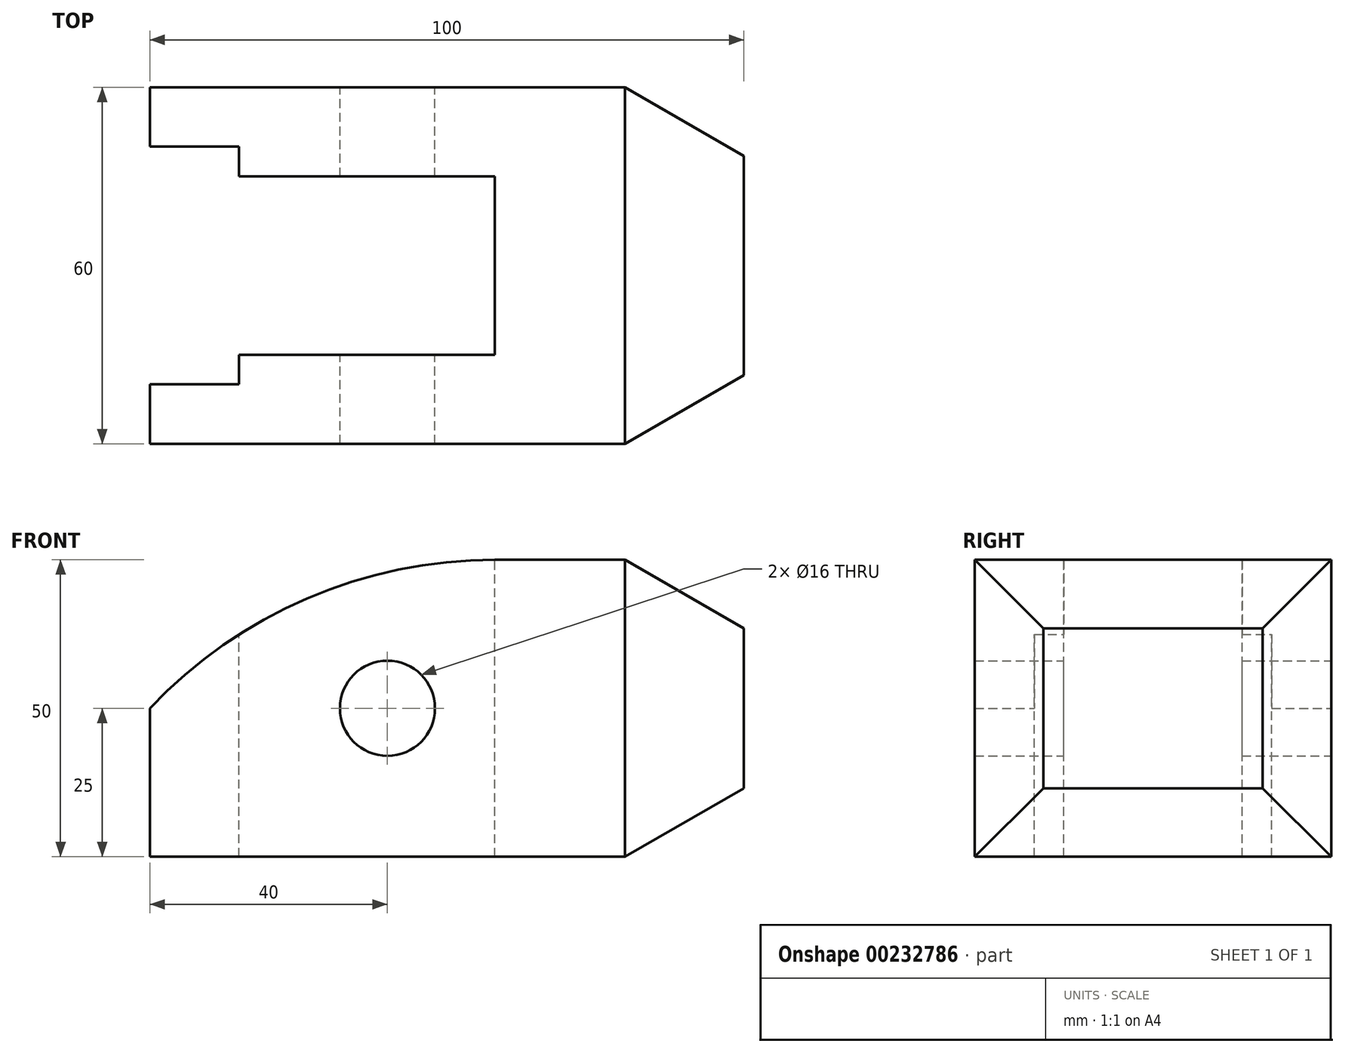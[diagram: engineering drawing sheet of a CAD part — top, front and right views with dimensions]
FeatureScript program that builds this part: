
annotation { "Feature Type Name" : "Feature", "Feature Type Description" : "" }
export const myFeature = defineFeature(function(context is Context, id is Id, definition is map)
    precondition{}
    {
        {
            var Q0;
            Q0=qCreatedBy(makeId("Front.planeOp"),FACE);
            var sketch = newSketch(context, id + "F0", { "sketchPlane" : qUnion([Q0])});
            skLineSegment(sketch, "E0.bottom", {"start": v(0, 0) * mm, "end": v(-80, 0) * mm});
            skLineSegment(sketch, "E0.top", {"start": v(0, 50) * mm, "end": v(-21.9, 50) * mm});
            skLineSegment(sketch, "E0.left", {"start": v(0, 0) * mm, "end": v(0, 50) * mm});
            skLineSegment(sketch, "E0.right", {"start": v(-80, 0) * mm, "end": v(-80, 25) * mm});
            skCircle(sketch, "E1", {"center": v(-40, 25) * mm, "radius": 8 * mm});
            skArc(sketch, "E2", {"start": v(-21.9, 50) * mm, "mid": v(-53.53, 43.48) * mm, "end": v(-80, 25) * mm});
            skLineSegment(sketch, "E3", {"start": v(-80, 25) * mm, "end": v(0, 25) * mm, "construction": true});
            skSolve(sketch);
        }
        {
            var Q0;
            Q0 = qSketchRegion(id + "F0", true);
            extrude(context, id + "F1", {"entities" : qUnion([Q0]), "depth" : 60 * mm});
        }
        {
            var Q0;
            Q0=makeQuery(id+"F1.opExtrude","SWEPT_FACE",FACE,{"disambiguationData":[OSD([sQuery(id+"F0.wireOp",EDGE,"E0.top")])]});
            var sketch = newSketch(context, id + "F2", { "sketchPlane" : qUnion([Q0])});
            skLineSegment(sketch, "E4.0", {"start": v(0, 0) * mm, "end": v(-21.9, 0) * mm, "construction": true});
            skLineSegment(sketch, "E5.0.0", {"start": v(-21.9, 0) * mm, "end": v(-80, 0) * mm, "construction": true});
            skLineSegment(sketch, "E5.0.1", {"start": v(-80, 0) * mm, "end": v(-80, -60) * mm, "construction": true});
            skLineSegment(sketch, "E5.0.2", {"start": v(-80, -60) * mm, "end": v(-21.9, -60) * mm, "construction": true});
            skLineSegment(sketch, "E5.0.3", {"start": v(-21.9, -60) * mm, "end": v(-21.9, 0) * mm, "construction": true});
            skLineSegment(sketch, "E6.0.1", {"start": v(-21.9, 0) * mm, "end": v(-21.9, -60) * mm, "construction": true});
            skLineSegment(sketch, "E6.0.2", {"start": v(-21.9, -60) * mm, "end": v(0, -60) * mm, "construction": true});
            skLineSegment(sketch, "E6.0.3", {"start": v(0, -60) * mm, "end": v(0, 0) * mm, "construction": true});
            skLineSegment(sketch, "E7", {"start": v(0, -30) * mm, "end": v(-80, -30) * mm, "construction": true});
            skLineSegment(sketch, "E8.bottom", {"start": v(-80, -15) * mm, "end": v(-15, -15) * mm});
            skLineSegment(sketch, "E8.top", {"start": v(-80, -45) * mm, "end": v(-15, -45) * mm});
            skLineSegment(sketch, "E8.left", {"start": v(-80, -15) * mm, "end": v(-80, -45) * mm});
            skLineSegment(sketch, "E8.right", {"start": v(-15, -15) * mm, "end": v(-15, -45) * mm});
            skLineSegment(sketch, "E9.top", {"start": v(-80, -10) * mm, "end": v(-65, -10) * mm});
            skLineSegment(sketch, "E9.left", {"start": v(-80, -15) * mm, "end": v(-80, -10) * mm});
            skLineSegment(sketch, "E9.right", {"start": v(-65, -15) * mm, "end": v(-65, -10) * mm});
            skLineSegment(sketch, "E10.top", {"start": v(-80, -50) * mm, "end": v(-65, -50) * mm});
            skLineSegment(sketch, "E10.left", {"start": v(-80, -45) * mm, "end": v(-80, -50) * mm});
            skLineSegment(sketch, "E10.right", {"start": v(-65, -45) * mm, "end": v(-65, -50) * mm});
            skSolve(sketch);
        }
        {
            var Q0;
            Q0=makeQuery(id+"F2.imprint","IMPRINT",FACE,{"disambiguationData":[TD([[makeQuery(id+"F2.imprint","IMPRINT",EDGE,{"derivedFrom":sQuery(id+"F2.wireOp",EDGE,"E9.top")}),-1.0]])]});
            var Q1;
            {var subQ4=sQuery(id+"F2.wireOp",EDGE,"E8.left");Q1=makeQuery(id+"F2.imprint","IMPRINT",FACE,{"disambiguationData":[TD([[makeQuery(id+"F2.imprint","IMPRINT",EDGE,{"derivedFrom":subQ4}),1.0]])]});}
            var Q2;
            Q2=makeQuery(id+"F2.imprint","IMPRINT",FACE,{"disambiguationData":[TD([[makeQuery(id+"F2.imprint","IMPRINT",EDGE,{"derivedFrom":sQuery(id+"F2.wireOp",EDGE,"E10.top")}),1.0]])]});
            extrude(context, id + "F3", {"entities" : qUnion([Q0, Q1, Q2]), "operationType" : NewBodyOperationType.REMOVE, "endBound" : BoundingType.THROUGH_ALL, "oppositeDirection" : true, "depth" : 25 * mm});
        }
        {
            var Q0;
            Q0=makeQuery(id+"F1.opExtrude","SWEPT_FACE",FACE,{"disambiguationData":[OSD([sQuery(id+"F0.wireOp",EDGE,"E0.left")])]});
            extrude(context, id + "F4", {"entities" : qUnion([Q0]), "operationType" : NewBodyOperationType.ADD, "depth" : 20 * mm});
        }
        {
            var Q0;
            {var subQ0=sQuery(id+"F0.wireOp",EDGE,"E0.top");Q0=makeQuery(id+"F4.boolean.opBoolean","MERGE",FACE,{"derivedFrom":[makeQuery(id+"F1.opExtrude","SWEPT_FACE",FACE,{"disambiguationData":[OSD([subQ0])]}),makeQuery(id+"F4.opExtrude","SWEPT_FACE",FACE,{"disambiguationData":[OSD([subQ0,sQuery(id+"F0.wireOp",EDGE,"E0.left")])]})]});}
            var sketch = newSketch(context, id + "F5", { "sketchPlane" : qUnion([Q0])});
            skLineSegment(sketch, "E11.0", {"start": v(20, -60) * mm, "end": v(20, 0) * mm, "construction": true});
            skLineSegment(sketch, "E12.0", {"start": v(20, 0) * mm, "end": v(-21.9, 0) * mm, "construction": true});
            skLineSegment(sketch, "E13.0", {"start": v(20, -60) * mm, "end": v(-21.9, -60) * mm, "construction": true});
            skLineSegment(sketch, "E14", {"start": v(0, 0) * mm, "end": v(20, -11.55) * mm});
            skLineSegment(sketch, "E15", {"start": v(0, 0) * mm, "end": v(0, -60) * mm, "construction": true});
            skLineSegment(sketch, "E16", {"start": v(0, -60) * mm, "end": v(20, -48.45) * mm});
            skLineSegment(sketch, "E17", {"start": v(0, 0) * mm, "end": v(20, 0) * mm});
            skLineSegment(sketch, "E18", {"start": v(20, -11.55) * mm, "end": v(20, 0) * mm});
            skLineSegment(sketch, "E19", {"start": v(20, -48.45) * mm, "end": v(20, -60) * mm});
            skLineSegment(sketch, "E20", {"start": v(0, -60) * mm, "end": v(20, -60) * mm});
            skSolve(sketch);
        }
        {
            var Q0;
            Q0=makeQuery(id+"F5.imprint","IMPRINT",FACE,{"disambiguationData":[TD([[makeQuery(id+"F5.imprint","IMPRINT",EDGE,{"derivedFrom":sQuery(id+"F5.wireOp",EDGE,"E14")}),1.0]])]});
            var Q1;
            Q1=makeQuery(id+"F5.imprint","IMPRINT",FACE,{"disambiguationData":[TD([[makeQuery(id+"F5.imprint","IMPRINT",EDGE,{"derivedFrom":sQuery(id+"F5.wireOp",EDGE,"E16")}),-1.0]])]});
            extrude(context, id + "F6", {"entities" : qUnion([Q0, Q1]), "operationType" : NewBodyOperationType.REMOVE, "endBound" : BoundingType.THROUGH_ALL, "oppositeDirection" : true, "depth" : 25 * mm});
        }
        {
            var Q0;
            {var subQ0=sQuery(id+"F0.wireOp",EDGE,"E0.left");Q0=makeQuery(id+"F4.boolean.opBoolean","MERGE",FACE,{"derivedFrom":[makeQuery(id+"F1.opExtrude","CAP_FACE",FACE,{"disambiguationData":[OSD([sQuery(id+"F0.wireOp",EDGE,"E0.bottom"),sQuery(id+"F0.wireOp",EDGE,"E0.top"),subQ0,sQuery(id+"F0.wireOp",EDGE,"E0.right"),sQuery(id+"F0.wireOp",EDGE,"E1"),sQuery(id+"F0.wireOp",EDGE,"E2")])],"isStart":false}),makeQuery(id+"F4.opExtrude","SWEPT_FACE",FACE,{"disambiguationData":[OSD([subQ0]),TDD([makeQuery(id+"F1.opExtrude","CAP_EDGE",EDGE,{"disambiguationData":[OSD([subQ0])],"isStart":false})])]})]});}
            var sketch = newSketch(context, id + "F7", { "sketchPlane" : qUnion([Q0])});
            skLineSegment(sketch, "E21.0.0", {"start": v(20, 0) * mm, "end": v(20, 50) * mm, "construction": true});
            skLineSegment(sketch, "E21.0.1", {"start": v(20, 50) * mm, "end": v(0, 50) * mm, "construction": true});
            skLineSegment(sketch, "E21.0.2", {"start": v(0, 50) * mm, "end": v(0, 0) * mm, "construction": true});
            skLineSegment(sketch, "E21.0.3", {"start": v(0, 0) * mm, "end": v(20, 0) * mm, "construction": true});
            skLineSegment(sketch, "E22", {"start": v(0, 50) * mm, "end": v(20, 38.45) * mm});
            skLineSegment(sketch, "E23", {"start": v(20, 38.45) * mm, "end": v(20, 50) * mm});
            skLineSegment(sketch, "E24", {"start": v(0, 0) * mm, "end": v(20, 11.55) * mm});
            skLineSegment(sketch, "E25", {"start": v(20, 11.55) * mm, "end": v(20, 0) * mm});
            skLineSegment(sketch, "E26", {"start": v(0, 50) * mm, "end": v(20, 50) * mm});
            skLineSegment(sketch, "E27", {"start": v(20, 0) * mm, "end": v(0, 0) * mm});
            skSolve(sketch);
        }
        {
            var Q0;
            Q0 = qSketchRegion(id + "F7", true);
            extrude(context, id + "F8", {"entities" : qUnion([Q0]), "operationType" : NewBodyOperationType.REMOVE, "endBound" : BoundingType.THROUGH_ALL, "oppositeDirection" : true, "depth" : 25 * mm});
        }
    });
